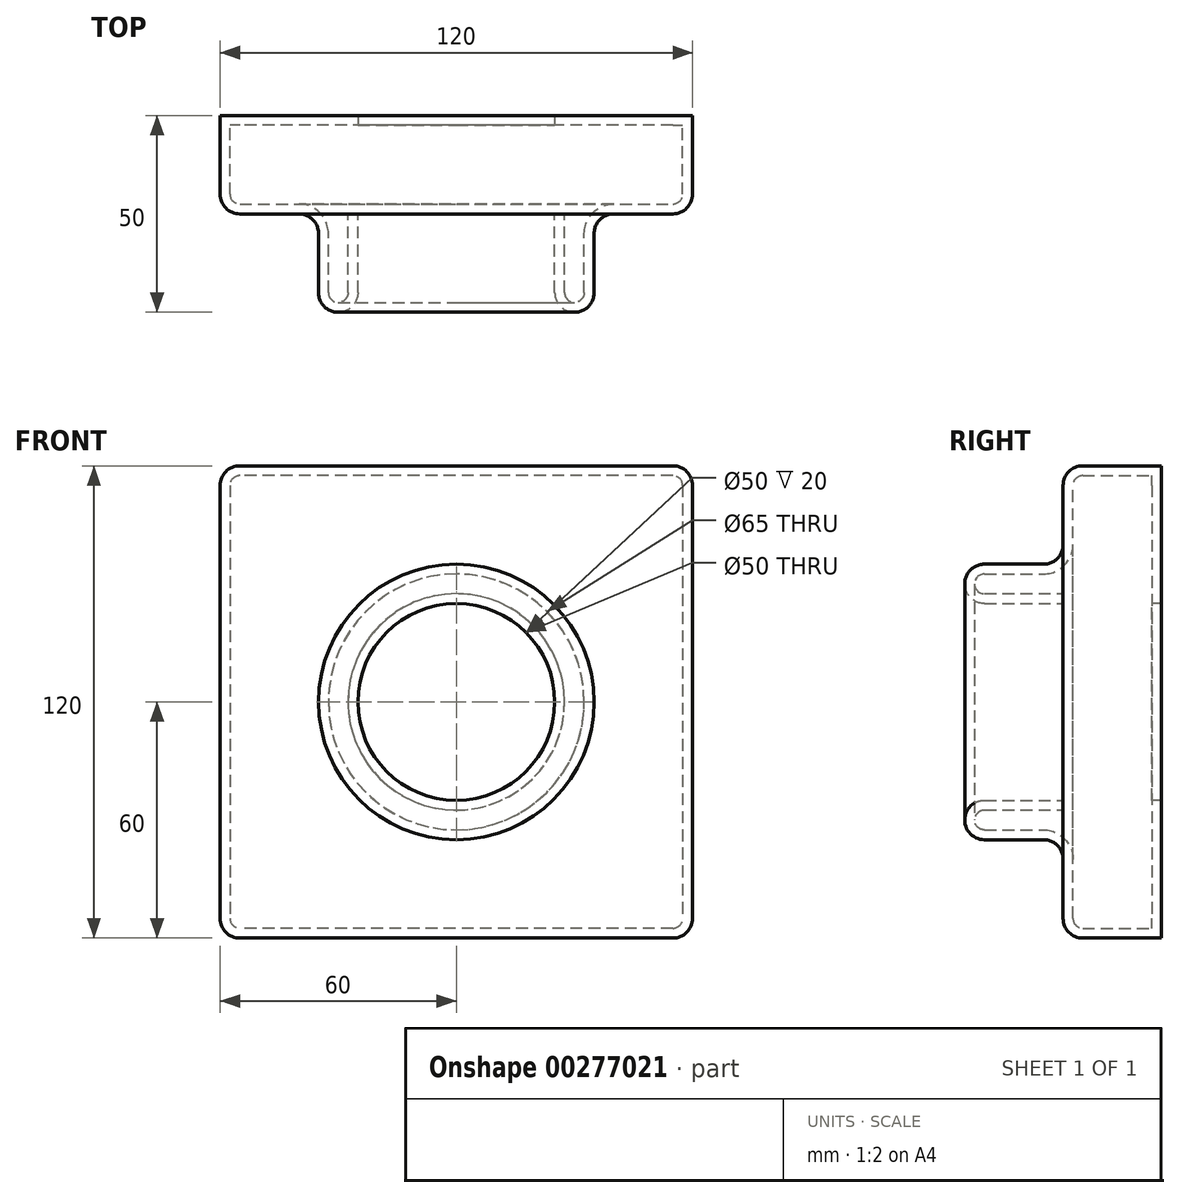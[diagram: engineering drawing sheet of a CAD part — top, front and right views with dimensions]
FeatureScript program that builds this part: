
annotation { "Feature Type Name" : "Feature", "Feature Type Description" : "" }
export const myFeature = defineFeature(function(context is Context, id is Id, definition is map)
    precondition{}
    {
        {
            var Q0;
            Q0=qCreatedBy(makeId("Front.planeOp"),FACE);
            var sketch = newSketch(context, id + "F0", { "sketchPlane" : qUnion([Q0])});
            skLineSegment(sketch, "E0.bottom", {"start": v(60, 60) * mm, "end": v(-60, 60) * mm});
            skLineSegment(sketch, "E0.top", {"start": v(60, -60) * mm, "end": v(-60, -60) * mm});
            skLineSegment(sketch, "E0.left", {"start": v(60, 60) * mm, "end": v(60, -60) * mm});
            skLineSegment(sketch, "E0.right", {"start": v(-60, 60) * mm, "end": v(-60, -60) * mm});
            skPoint(sketch, "E0.middle", {"position": v(0, 0) * mm});
            skSolve(sketch);
        }
        {
            var Q0;
            Q0 = qSketchRegion(id + "F0", true);
            extrude(context, id + "F1", {"entities" : qUnion([Q0]), "depth" : 25 * mm});
        }
        {
            var Q0;
            Q0=makeQuery(id+"F1.opExtrude","SWEPT_EDGE",EDGE,{"disambiguationData":[OSD([sQuery(id+"F0.wireOp",EDGE,"E0.bottom"),sQuery(id+"F0.wireOp",EDGE,"E0.right")])]});
            var Q1;
            Q1=makeQuery(id+"F1.opExtrude","SWEPT_EDGE",EDGE,{"disambiguationData":[OSD([sQuery(id+"F0.wireOp",EDGE,"E0.bottom"),sQuery(id+"F0.wireOp",EDGE,"E0.left")])]});
            var Q2;
            Q2=makeQuery(id+"F1.opExtrude","SWEPT_EDGE",EDGE,{"disambiguationData":[OSD([sQuery(id+"F0.wireOp",EDGE,"E0.top"),sQuery(id+"F0.wireOp",EDGE,"E0.left")])]});
            var Q3;
            Q3=makeQuery(id+"F1.opExtrude","SWEPT_EDGE",EDGE,{"disambiguationData":[OSD([sQuery(id+"F0.wireOp",EDGE,"E0.top"),sQuery(id+"F0.wireOp",EDGE,"E0.right")])]});
            fillet(context, id + "F2", {"entities" : qUnion([Q0, Q1, Q2, Q3]), "radius" : 5 * mm, "tangentPropagation" : true, "allowEdgeOverflow" : false});
        }
        {
            var Q0;
            Q0=makeQuery(id+"F1.opExtrude","CAP_FACE",FACE,{"disambiguationData":[OSD([sQuery(id+"F0.wireOp",EDGE,"E0.bottom"),sQuery(id+"F0.wireOp",EDGE,"E0.top"),sQuery(id+"F0.wireOp",EDGE,"E0.left"),sQuery(id+"F0.wireOp",EDGE,"E0.right")])],"isStart":false});
            var sketch = newSketch(context, id + "F3", { "sketchPlane" : qUnion([Q0])});
            skCircle(sketch, "E1", {"center": v(0, 0) * mm, "radius": 35 * mm});
            skCircle(sketch, "E2", {"center": v(0, 0) * mm, "radius": 25 * mm});
            skSolve(sketch);
        }
        {
            var Q0;
            Q0 = qSketchRegion(id + "F3", true);
            extrude(context, id + "F4", {"entities" : qUnion([Q0]), "operationType" : NewBodyOperationType.ADD, "depth" : 25 * mm});
        }
        {
            var Q0;
            Q0=makeQuery(id+"F1.opExtrude","CAP_EDGE",EDGE,{"disambiguationData":[OSD([sQuery(id+"F0.wireOp",EDGE,"E0.right")])],"isStart":false});
            var Q1;
            Q1=makeQuery(id+"F1.opExtrude","CAP_EDGE",EDGE,{"disambiguationData":[OSD([sQuery(id+"F0.wireOp",EDGE,"E0.top")])],"isStart":false});
            var Q2;
            Q2=makeQuery(id+"F4.opExtrude","CAP_FACE",FACE,{"disambiguationData":[OSD([sQuery(id+"F3.wireOp",EDGE,"E1"),sQuery(id+"F3.wireOp",EDGE,"E2")])],"isStart":false});
            var Q3;
            Q3=makeQuery(id+"F4.opExtrude","SWEPT_FACE",FACE,{"disambiguationData":[OSD([sQuery(id+"F3.wireOp",EDGE,"E1")])]});
            fillet(context, id + "F5", {"entities" : qUnion([Q0, Q1, Q2, Q3]), "radius" : 5 * mm, "tangentPropagation" : true, "allowEdgeOverflow" : false});
        }
        {
            var Q0;
            Q0=makeQuery(id+"F4.boolean.opBoolean","SPLIT",FACE,{"disambiguationData":[TD([makeQuery(id+"F4.opExtrude","SWEPT_FACE",FACE,{"disambiguationData":[OSD([sQuery(id+"F3.wireOp",EDGE,"E2")])]})])],"derivedFrom":makeQuery(id+"F1.opExtrude","CAP_FACE",FACE,{"disambiguationData":[OSD([sQuery(id+"F0.wireOp",EDGE,"E0.bottom"),sQuery(id+"F0.wireOp",EDGE,"E0.top"),sQuery(id+"F0.wireOp",EDGE,"E0.left"),sQuery(id+"F0.wireOp",EDGE,"E0.right")])],"isStart":false})});
            shell(context, id + "F6", {"entities" : qUnion([Q0]), "thickness" : 2.5 * mm});
        }
        {
            var Q0;
            {var subQ0=sQuery(id+"F0.wireOp",EDGE,"E0.right");var subQ1=sQuery(id+"F0.wireOp",EDGE,"E0.left");var subQ2=sQuery(id+"F0.wireOp",EDGE,"E0.top");var subQ3=sQuery(id+"F0.wireOp",EDGE,"E0.bottom");Q0=makeQuery(id+"F6.opShell","OFFSET_FACE",FACE,{"disambiguationData":[OSD([subQ3,subQ2,subQ1,subQ0]),TDD([makeQuery(id+"F1.opExtrude","CAP_FACE",FACE,{"disambiguationData":[OSD([subQ3,subQ2,subQ1,subQ0])],"isStart":true})])]});}
            var sketch = newSketch(context, id + "F7", { "sketchPlane" : qUnion([Q0])});
            skCircle(sketch, "E3", {"center": v(0, 0) * mm, "radius": 25 * mm});
            skSolve(sketch);
        }
        {
            var Q0;
            Q0 = qSketchRegion(id + "F7", true);
            extrude(context, id + "F8", {"entities" : qUnion([Q0]), "operationType" : NewBodyOperationType.REMOVE, "endBound" : BoundingType.THROUGH_ALL, "oppositeDirection" : true, "depth" : 25 * mm});
        }
    });
